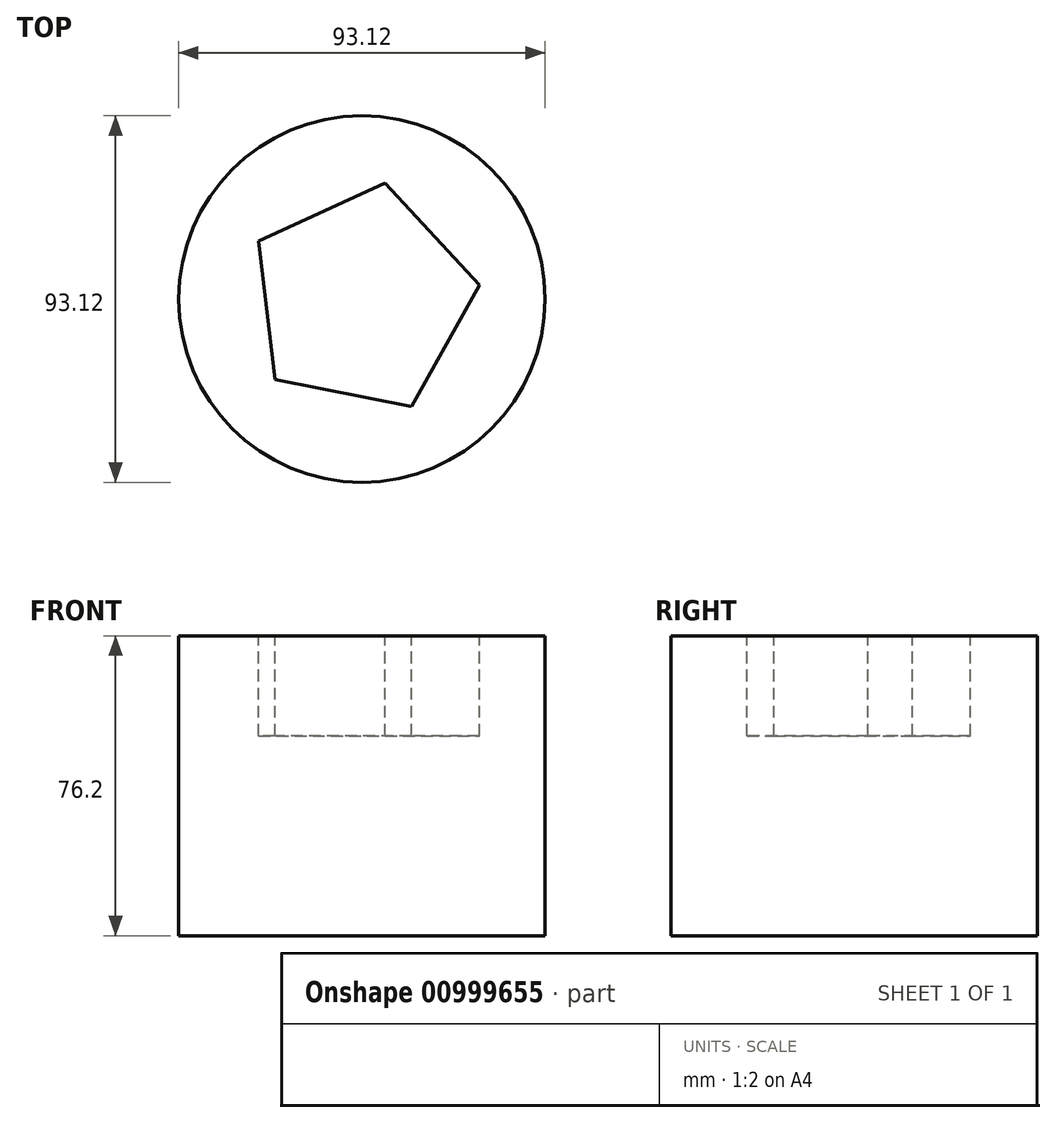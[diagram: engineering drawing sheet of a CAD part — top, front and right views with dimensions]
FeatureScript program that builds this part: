
annotation { "Feature Type Name" : "Feature", "Feature Type Description" : "" }
export const myFeature = defineFeature(function(context is Context, id is Id, definition is map)
    precondition{}
    {
        {
            var Q0;
            Q0=qCreatedBy(makeId("Top.planeOp"),FACE);
            var sketch = newSketch(context, id + "F0", { "sketchPlane" : qUnion([Q0])});
            skCircle(sketch, "E0", {"center": v(0, 0) * mm, "radius": 46.56 * mm});
            skSolve(sketch);
        }
        {
            var Q0;
            Q0=makeQuery(id+"F0.imprint","IMPRINT",FACE,{"disambiguationData":[TD([[makeQuery(id+"F0.imprint","IMPRINT",EDGE,{"derivedFrom":sQuery(id+"F0.wireOp",EDGE,"E0")}),1.0]])]});
            extrude(context, id + "F1", {"entities" : qUnion([Q0]), "depth" : 25.4 * mm, "offsetDistance" : 25.4 * mm});
        }
        {
            var Q0;
            Q0=makeQuery(id+"F1.opExtrude","CAP_FACE",FACE,{"disambiguationData":[OSD([sQuery(id+"F0.wireOp",EDGE,"E0")])],"isStart":false});
            var sketch = newSketch(context, id + "F2", { "sketchPlane" : qUnion([Q0])});
            skSolve(sketch);
        }
        {
            var Q0;
            Q0=makeQuery(id+"F2.imprint","IMPRINT",FACE,{"disambiguationData":[TD([[makeQuery(id+"F2.imprint","IMPRINT",EDGE,{"derivedFrom":makeQuery(id+"F1.opExtrude","CAP_EDGE",EDGE,{"disambiguationData":[OSD([sQuery(id+"F0.wireOp",EDGE,"E0")])],"isStart":false})}),1.0]])]});
            extrude(context, id + "F3", {"entities" : qUnion([Q0]), "operationType" : NewBodyOperationType.ADD, "depth" : 25.4 * mm, "offsetDistance" : 25.4 * mm, "hasSecondDirection" : true, "secondDirectionOppositeDirection" : true, "secondDirectionDepth" : 25.4 * mm});
        }
        {
            var Q0;
            Q0=makeQuery(id+"F3.opExtrude","CAP_FACE",FACE,{"disambiguationData":[OSD([sQuery(id+"F0.wireOp",EDGE,"E0")])],"isStart":false});
            var sketch = newSketch(context, id + "F4", { "sketchPlane" : qUnion([Q0])});
            skSolve(sketch);
        }
        {
            var Q0;
            Q0=makeQuery(id+"F4.imprint","IMPRINT",FACE,{"disambiguationData":[TD([[makeQuery(id+"F4.imprint","IMPRINT",EDGE,{"derivedFrom":makeQuery(id+"F3.opExtrude","CAP_EDGE",EDGE,{"disambiguationData":[OSD([sQuery(id+"F0.wireOp",EDGE,"E0")])],"isStart":false})}),1.0]])]});
            extrude(context, id + "F5", {"entities" : qUnion([Q0]), "operationType" : NewBodyOperationType.ADD, "depth" : 25.4 * mm, "offsetDistance" : 25.4 * mm});
        }
        {
            var Q0;
            Q0=makeQuery(id+"F5.opExtrude","CAP_FACE",FACE,{"disambiguationData":[OSD([sQuery(id+"F0.wireOp",EDGE,"E0")])],"isStart":false});
            var sketch = newSketch(context, id + "F6", { "sketchPlane" : qUnion([Q0])});
            skCircle(sketch, "E1.cCircle", {"center": v(0, 0) * mm, "radius": 24.33 * mm, "construction": true});
            skLineSegment(sketch, "E1.0", {"start": v(29.87, 3.5) * mm, "end": v(12.57, -27.32) * mm});
            skLineSegment(sketch, "E1.1", {"start": v(12.57, -27.32) * mm, "end": v(-22.1, -20.4) * mm});
            skLineSegment(sketch, "E1.2", {"start": v(-22.1, -20.4) * mm, "end": v(-26.22, 14.72) * mm});
            skLineSegment(sketch, "E1.3", {"start": v(-26.22, 14.72) * mm, "end": v(5.9, 29.49) * mm});
            skLineSegment(sketch, "E1.4", {"start": v(5.9, 29.49) * mm, "end": v(29.87, 3.5) * mm});
            skPoint(sketch, "E1.0.midPoint", {"position": v(21.22, -11.9) * mm});
            skSolve(sketch);
        }
        {
            var Q0;
            Q0=makeQuery(id+"F6.imprint","IMPRINT",FACE,{"disambiguationData":[TD([[makeQuery(id+"F6.imprint","IMPRINT",EDGE,{"derivedFrom":sQuery(id+"F6.wireOp",EDGE,"E1.0")}),-1.0]])]});
            var sketch = newSketch(context, id + "F7", { "sketchPlane" : qUnion([Q0])});
            skSolve(sketch);
        }
        {
            var Q0;
            Q0=makeQuery(id+"F6.imprint","IMPRINT",FACE,{"disambiguationData":[TD([[makeQuery(id+"F6.imprint","IMPRINT",EDGE,{"derivedFrom":sQuery(id+"F6.wireOp",EDGE,"E1.0")}),-1.0]])]});
            extrude(context, id + "F8", {"entities" : qUnion([Q0]), "operationType" : NewBodyOperationType.REMOVE, "oppositeDirection" : true, "depth" : 25.4 * mm, "offsetDistance" : 25.4 * mm});
        }
        {
            var Q0;
            Q0=makeQuery(id+"F7.imprint","IMPRINT",FACE,{"disambiguationData":[TD([[makeQuery(id+"F7.imprint","IMPRINT",EDGE,{"derivedFrom":makeQuery(id+"F6.imprint","IMPRINT",EDGE,{"derivedFrom":sQuery(id+"F6.wireOp",EDGE,"E1.0")})}),-1.0]])]});
            extrude(context, id + "F9", {"entities" : qUnion([Q0]), "operationType" : NewBodyOperationType.REMOVE, "oppositeDirection" : true, "depth" : 25.4 * mm, "offsetDistance" : 25.4 * mm});
        }
    });
